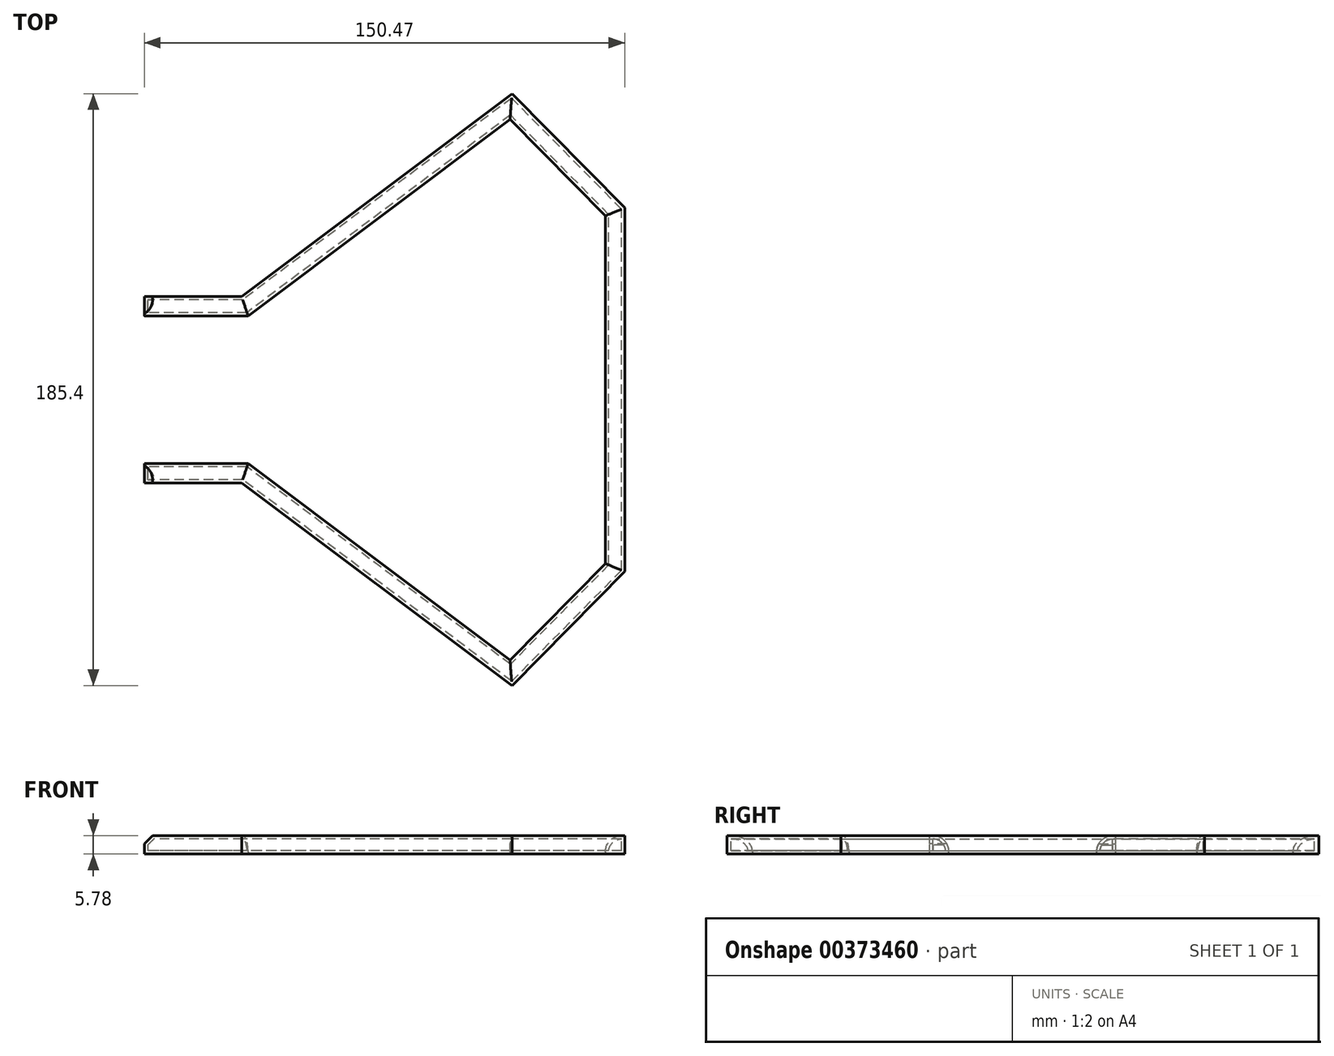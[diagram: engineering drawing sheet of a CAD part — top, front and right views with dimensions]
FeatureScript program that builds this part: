
annotation { "Feature Type Name" : "Feature", "Feature Type Description" : "" }
export const myFeature = defineFeature(function(context is Context, id is Id, definition is map)
    precondition{}
    {
        {
            var Q0;
            Q0=qCreatedBy(makeId("Top.planeOp"),FACE);
            var sketch = newSketch(context, id + "F0", { "sketchPlane" : qUnion([Q0])});
            skLineSegment(sketch, "E0", {"start": v(0, 0) * mm, "end": v(0, 55.72) * mm});
            skLineSegment(sketch, "E1", {"start": v(0, 55.72) * mm, "end": v(-32.6, 88.69) * mm});
            skLineSegment(sketch, "E2", {"start": v(-32.6, 88.69) * mm, "end": v(-115.98, 26.15) * mm});
            skLineSegment(sketch, "E3", {"start": v(-115.98, 26.15) * mm, "end": v(-147.44, 26.15) * mm});
            skSolve(sketch);
        }
        {
            var Q0;
            Q0=qCreatedBy(makeId("Front.planeOp"),FACE);
            var sketch = newSketch(context, id + "F1", { "sketchPlane" : qUnion([Q0])});
            skLineSegment(sketch, "E4.bottom", {"start": v(3.03, -2.89) * mm, "end": v(-3.03, -2.89) * mm});
            skLineSegment(sketch, "E4.top", {"start": v(3.03, 2.89) * mm, "end": v(-3.03, 2.89) * mm});
            skLineSegment(sketch, "E4.left", {"start": v(3.03, -2.89) * mm, "end": v(3.03, 2.89) * mm});
            skLineSegment(sketch, "E4.right", {"start": v(-3.03, -2.89) * mm, "end": v(-3.03, 2.89) * mm});
            skPoint(sketch, "E4.middle", {"position": v(0, 0) * mm});
            skSolve(sketch);
        }
        {
            var Q0;
            Q0=makeQuery(id+"F1.imprint","IMPRINT",FACE,{"disambiguationData":[TD([[makeQuery(id+"F1.imprint","IMPRINT",EDGE,{"derivedFrom":sQuery(id+"F1.wireOp",EDGE,"E4.bottom")}),-1.0]])]});
            var Q1;
            Q1=sQuery(id+"F0.wireOp",EDGE,"E0");
            var Q2;
            Q2=sQuery(id+"F0.wireOp",EDGE,"E1");
            var Q3;
            Q3=sQuery(id+"F0.wireOp",EDGE,"E2");
            var Q4;
            Q4=sQuery(id+"F0.wireOp",EDGE,"E3");
            sweep(context, id + "F2", {"profiles" : qUnion([Q0]), "path" : qUnion([Q1, Q2, Q3, Q4])});
        }
        {
            var Q0;
            Q0=makeQuery(id+"F2.opSweep","CAP_EDGE",EDGE,{"disambiguationData":[OSD([sQuery(id+"F0.wireOp",VERTEX,"E3.end"),sQuery(id+"F1.wireOp",EDGE,"E4.top")])],"isStart":false});
            chamfer(context, id + "F3", {"entities" : qUnion([Q0]), "width" : 2.54 * mm, "tangentPropagation" : true});
        }
        {
            var Q0;
            Q0=makeQuery(id+"F2.opSweep","SWEPT_EDGE",EDGE,{"disambiguationData":[OSD([sQuery(id+"F0.wireOp",EDGE,"E3"),sQuery(id+"F1.wireOp",EDGE,"E4.top"),sQuery(id+"F1.wireOp",EDGE,"E4.right")])]});
            var Q1;
            Q1=makeQuery(id+"F2.opSweep","SWEPT_EDGE",EDGE,{"disambiguationData":[OSD([sQuery(id+"F0.wireOp",EDGE,"E2"),sQuery(id+"F1.wireOp",EDGE,"E4.top"),sQuery(id+"F1.wireOp",EDGE,"E4.right")])]});
            var Q2;
            Q2=makeQuery(id+"F2.opSweep","SWEPT_EDGE",EDGE,{"disambiguationData":[OSD([sQuery(id+"F0.wireOp",EDGE,"E1"),sQuery(id+"F1.wireOp",EDGE,"E4.top"),sQuery(id+"F1.wireOp",EDGE,"E4.right")])]});
            var Q3;
            Q3=makeQuery(id+"F2.opSweep","SWEPT_EDGE",EDGE,{"disambiguationData":[OSD([sQuery(id+"F0.wireOp",EDGE,"E0"),sQuery(id+"F1.wireOp",EDGE,"E4.top"),sQuery(id+"F1.wireOp",EDGE,"E4.right")])]});
            fillet(context, id + "F4", {"entities" : qUnion([Q0, Q1, Q2, Q3]), "radius" : 5.08 * mm, "tangentPropagation" : true, "allowEdgeOverflow" : false});
        }
        {
            var Q0;
            Q0=makeQuery(id+"F2.opSweep","CAP_FACE",FACE,{"disambiguationData":[OSD([sQuery(id+"F0.wireOp",VERTEX,"E0.start"),sQuery(id+"F1.wireOp",EDGE,"E4.bottom"),sQuery(id+"F1.wireOp",EDGE,"E4.top"),sQuery(id+"F1.wireOp",EDGE,"E4.left"),sQuery(id+"F1.wireOp",EDGE,"E4.right")])],"isStart":true});
            shell(context, id + "F5", {"entities" : qUnion([Q0]), "thickness" : 1.02 * mm});
        }
        {
            var Q0;
            Q0=makeQuery(id+"F2.opSweep","SWEPT_BODY",BODY,{"disambiguationData":[OSD([sQuery(id+"F0.wireOp",EDGE,"E3"),sQuery(id+"F1.wireOp",EDGE,"E4.bottom"),sQuery(id+"F1.wireOp",EDGE,"E4.top"),sQuery(id+"F1.wireOp",EDGE,"E4.left"),sQuery(id+"F1.wireOp",EDGE,"E4.right")])]});
            var Q1;
            Q1=qCreatedBy(makeId("Front.planeOp"),FACE);
            mirror(context, id + "F6", {"operationType" : NewBodyOperationType.ADD, "entities" : qUnion([Q0]), "mirrorPlane" : qUnion([Q1])});
        }
    });
